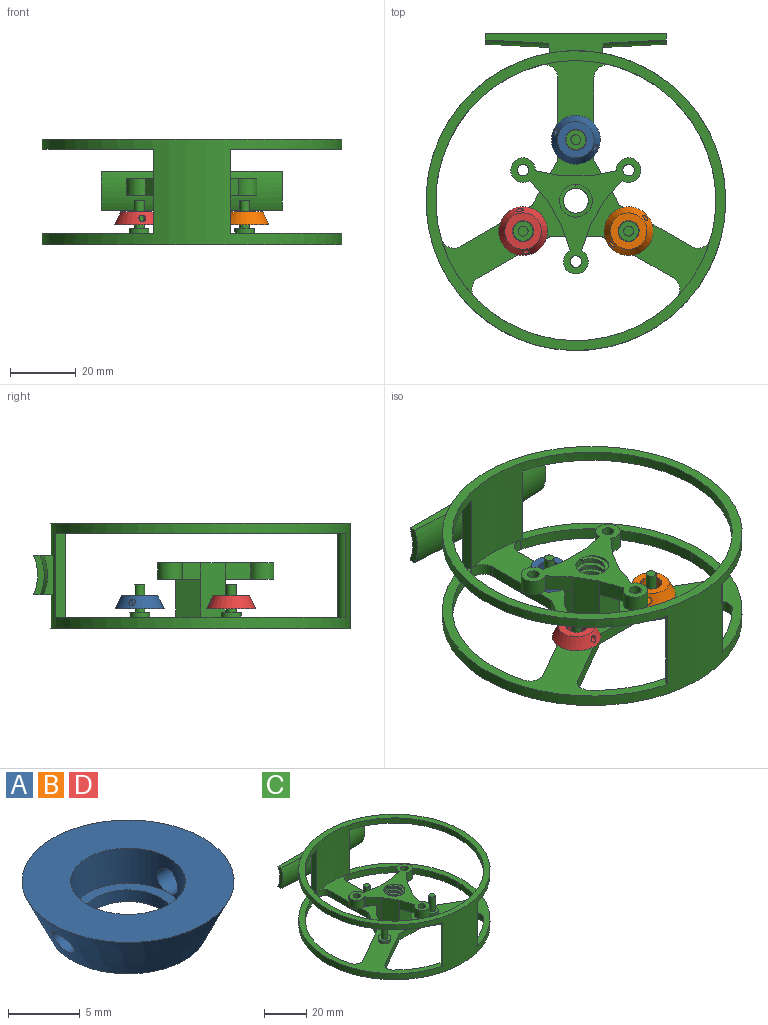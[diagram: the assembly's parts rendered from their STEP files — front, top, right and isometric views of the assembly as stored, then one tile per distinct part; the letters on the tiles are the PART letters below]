
ASSEMBLY  parts=4 mates=1
PART A: 8 faces, bbox 14.8x14.8x4 mm
  f0: cone r=7.4mm half-angle=25deg, axis (0,0,1), area 172.4mm2, adj f2,f3,f6,f7
  f1: cylinder r=4mm len=8mm, axis (0,0,1), area 69.1mm2, adj f3,f4,f6,f7
  f2: plane 11.07x11.07mm, normal (0,0,-1), area 64mm2, adj f0,f5
  f3: plane 14.8x14.8mm, normal (0,0,1), area 121.7mm2, adj f0,f1
  f4: plane 8x8mm, normal (0,0,1), area 18.1mm2, adj f1,f5
  f5: cylinder r=3.2mm len=6.4mm, axis (0,0,1), area 20.1mm2, adj f2,f4
  f6: cylinder r=1mm len=3.06mm, axis (-1,0,0), area 15.7mm2, adj f0,f1
  f7: cylinder r=1mm len=3.06mm, axis (-1,0,0), area 15.6mm2, adj f0,f1
PART B: same geometry as A
PART C: 84 faces, bbox 91.6x96.8x32.6 mm
  f0: cylinder r=42.5mm len=85mm, axis (0,0,1), area 2464.3mm2, adj f1,f2,f3,f5,f6,f7,f8,f9
  f1: cylinder r=42.5mm len=11.51mm, axis (0,0,1), area 40.8mm2, adj f0,f6,f7,f79
  f2: plane 87.9x37.23mm, normal (0,0,-1), area 347.3mm2, adj f0,f4,f9,f10,f77
  f3: plane 87.9x37.23mm, normal (0,0,-1), area 347.3mm2, adj f0,f4,f8,f11,f76
  f4: cylinder r=45.5mm len=91mm, axis (0,0,1), area 2882.7mm2, adj f2,f3,f5,f6,f7,f8,f9,f10
  f5: plane 91x91mm, normal (0,0,1), area 829.4mm2, adj f0,f4
  f6: plane 91x87.9mm, normal (0,0,1), area 1898.5mm2, adj f0,f1,f4,f8,f9,f10,f11,f12
  f7: plane 91x91mm, normal (0,0,-1), area 2234.4mm2, adj f0,f1,f4,f15,f16,f17,f18,f19
  f8: plane 25.5x2.9mm, normal (0.97,-0.26,0), area 76.5mm2, adj f0,f3,f4,f6
  f9: plane 25.5x2.9mm, normal (-0.97,-0.26,0), area 76.5mm2, adj f0,f2,f4,f6
  f10: plane 25.5x0.1mm, normal (-0.97,0.26,0), area 2.5mm2, adj f2,f4,f6,f77
  f11: plane 25.5x0.1mm, normal (0.97,0.26,0), area 2.5mm2, adj f3,f4,f6,f76
  f12: plane 11.5x7.5mm, normal (-0.87,0.5,0), area 99.6mm2, adj f6,f49,f50,f66
  f13: plane 11.5x8.66mm, normal (0,-1,0), area 99.6mm2, adj f6,f50,f51,f61
  f14: plane 11.5x7.5mm, normal (0.87,0.5,0), area 99.6mm2, adj f6,f49,f51,f56
  f15: plane 15.53x3.5mm, normal (0,-1,0), area 54.3mm2, adj f6,f7,f16,f23
  f16: plane 21.8x12.59mm, normal (0.5,-0.87,0), area 88.1mm2, adj f6,f7,f15,f83
  f17: plane 21.8x12.59mm, normal (-0.5,0.87,0), area 88.1mm2, adj f6,f7,f18,f82
  f18: plane 13.45x7.76mm, normal (-0.87,0.5,0), area 54.3mm2, adj f6,f7,f17,f19
  f19: plane 25.17x3.5mm, normal (-1,0,0), area 88.1mm2, adj f6,f7,f18,f81
  f20: plane 25.17x3.5mm, normal (1,0,0), area 88.1mm2, adj f6,f7,f21,f80
  f21: plane 13.45x7.76mm, normal (0.87,0.5,0), area 54.3mm2, adj f6,f7,f20,f22
  f22: plane 21.8x12.59mm, normal (0.5,0.87,0), area 88.1mm2, adj f6,f7,f21,f79
  f23: plane 21.8x12.59mm, normal (-0.5,-0.87,0), area 88.1mm2, adj f6,f7,f15,f78
  f24: cylinder r=3mm len=6mm, axis (0,0,1), area 28.3mm2, adj f6,f25
  f25: plane 6x6mm, normal (0,0,1), area 21.2mm2, adj f24,f26
  f26: cylinder r=1.5mm len=8.5mm, axis (0,0,1), area 80.1mm2, adj f25,f27
  f27: plane 3x3mm, normal (0,0,1), area 7.1mm2, adj f26
  f28: cylinder r=3mm len=6mm, axis (0,0,1), area 28.3mm2, adj f6,f29
  f29: plane 6x6mm, normal (0,0,1), area 21.2mm2, adj f28,f30
  f30: cylinder r=1.5mm len=8.5mm, axis (0,0,1), area 80.1mm2, adj f29,f31
  f31: plane 3x3mm, normal (0,0,1), area 7.1mm2, adj f30
  f32: cylinder r=3mm len=6mm, axis (0,0,1), area 28.3mm2, adj f6,f33
  f33: plane 6x6mm, normal (0,0,1), area 21.2mm2, adj f32,f34
  f34: cylinder r=1.5mm len=8.5mm, axis (0,0,1), area 80.1mm2, adj f33,f35
  f35: plane 3x3mm, normal (0,0,1), area 7.1mm2, adj f34
  f36: plane 1.2x0.88mm, normal (-1,0,0), area 1.1mm2, adj f38,f39,f40,f41
  f37: plane 1.2x0.88mm, normal (1,0,0), area 1.1mm2, adj f38,f39,f40,f47
  f38: cylinder r=3.8mm len=15mm, axis (0,0,-1), area 125.6mm2, adj f36,f37,f39,f40
  f39: bspline ~14.12x11.55mm, area 199.8mm2, adj f36,f37,f38,f42,f43,f44,f45,f46
  f40: bspline ~14.12x11.55mm, area 199.8mm2, adj f36,f37,f38,f41,f42,f43,f44,f45
  f41: cylinder r=5mm len=10mm, axis (0,0,1), area 37mm2, adj f36,f40,f42,f48
  f42: cylinder r=5mm len=10mm, axis (0,0,1), area 46.4mm2, adj f39,f40,f41,f43
  f43: cylinder r=5mm len=10mm, axis (0,0,1), area 46.4mm2, adj f39,f40,f42,f44
  f44: cylinder r=5mm len=10mm, axis (0,0,1), area 46.4mm2, adj f39,f40,f43,f45
  f45: cylinder r=5mm len=10mm, axis (0,0,1), area 46.4mm2, adj f39,f40,f44,f46
  f46: cylinder r=5mm len=10mm, axis (0,0,1), area 46.4mm2, adj f39,f40,f45,f47
  f47: cylinder r=5mm len=10mm, axis (0,0,1), area 194.1mm2, adj f7,f37,f39,f46
  f48: plane 39.54x35.25mm, normal (0,0,1), area 357.1mm2, adj f41,f49,f50,f51,f52,f53,f54,f55
  f49: plane 16.5x8.66mm, normal (0,1,0), area 142.9mm2, adj f6,f12,f14,f48,f53,f65
  f50: plane 16.5x7.5mm, normal (-0.87,-0.5,0), area 142.9mm2, adj f6,f12,f13,f48,f60,f63
  f51: plane 16.5x7.5mm, normal (0.87,-0.5,0), area 142.9mm2, adj f6,f13,f14,f48,f55,f58
  f52: cylinder r=3.75mm len=7.5mm, axis (0,0,1), area 99.6mm2, adj f48,f53,f55,f56
  f53: plane 7.94x5mm, normal (-0.2,0.98,0), area 40.5mm2, adj f48,f49,f52,f56
  f54: cylinder r=1.75mm len=5mm, axis (0,0,1), area 55mm2, adj f48,f56
  f55: plane 6.08x5.36mm, normal (0.75,-0.66,0), area 40.5mm2, adj f48,f51,f52,f56
  f56: plane 15.44x13mm, normal (0,0,-1), area 80.2mm2, adj f14,f52,f53,f54,f55
  f57: cylinder r=3.75mm len=7.5mm, axis (0,0,1), area 99.6mm2, adj f48,f58,f60,f61
  f58: plane 7.68x5mm, normal (0.95,-0.32,0), area 40.5mm2, adj f48,f51,f57,f61
  f59: cylinder r=1.75mm len=5mm, axis (0,0,1), area 55mm2, adj f48,f61
  f60: plane 7.68x5mm, normal (-0.95,-0.32,0), area 40.5mm2, adj f48,f50,f57,f61
  f61: plane 14.75x8.66mm, normal (0,0,-1), area 80.2mm2, adj f13,f57,f58,f59,f60
  f62: cylinder r=3.75mm len=7.5mm, axis (0,0,1), area 99.6mm2, adj f48,f63,f65,f66
  f63: plane 6.08x5.36mm, normal (-0.75,-0.66,0), area 40.5mm2, adj f48,f50,f62,f66
  f64: cylinder r=1.75mm len=5mm, axis (0,0,1), area 55mm2, adj f48,f66
  f65: plane 7.94x5mm, normal (0.2,0.98,0), area 40.5mm2, adj f48,f49,f62,f66
  f66: plane 15.44x13mm, normal (0,0,-1), area 80.2mm2, adj f12,f62,f63,f64,f65
  f67: plane 55x5.94mm, normal (0,0,1), area 186.6mm2, adj f4,f69,f70,f71,f72,f73,f74,f75
  f68: plane 55x5.94mm, normal (0,0,-1), area 186.6mm2, adj f4,f69,f70,f71,f72,f73,f74,f75
  f69: plane 12.58x3.52mm, normal (0.98,-0.17,0), area 25.5mm2, adj f4,f67,f68,f74
  f70: plane 12.58x3.52mm, normal (-0.98,-0.17,0), area 25.5mm2, adj f4,f67,f68,f71
  f71: cylinder r=15mm len=19.15mm, axis (-1,0.05,0), area 235.5mm2, adj f67,f68,f70,f75
  f72: cylinder r=15mm len=55mm, axis (1,0,0), area 679mm2, adj f67,f68,f73,f75
  f73: plane 12.03x3.28mm, normal (1,0,0), area 24mm2, adj f67,f68,f72,f74
  f74: cylinder r=15mm len=19.15mm, axis (1,0.05,0), area 235.5mm2, adj f67,f68,f69,f73
  f75: plane 12.03x3.28mm, normal (-1,0,0), area 24mm2, adj f67,f68,f71,f72
  f76: cylinder r=3mm len=25.5mm, axis (0,0,1), area 115.1mm2, adj f0,f3,f6,f11
  f77: cylinder r=3mm len=25.5mm, axis (0,0,1), area 115.1mm2, adj f0,f2,f6,f10
  f78: cylinder r=4mm len=6.26mm, axis (0,0,1), area 25.5mm2, adj f0,f6,f7,f23
  f79: cylinder r=4mm len=5.85mm, axis (0,0,1), area 25.5mm2, adj f1,f6,f7,f22
  f80: cylinder r=4mm len=4.99mm, axis (0,0,1), area 25.5mm2, adj f0,f6,f7,f20
  f81: cylinder r=4mm len=4.99mm, axis (0,0,1), area 25.5mm2, adj f0,f6,f7,f19
  f82: cylinder r=4mm len=5.85mm, axis (0,0,1), area 25.5mm2, adj f0,f6,f7,f17
  f83: cylinder r=4mm len=6.26mm, axis (0,0,1), area 25.5mm2, adj f0,f6,f7,f16
PART D: same geometry as A
PLACE A rot(axis=(0.19,0.98,0),180deg) t=(-8.14,-1.47,4.22)mm
PLACE B rot(axis=(0.94,0.33,0),180deg) t=(3.15,2.47,4.22)mm
PLACE C t=(-1.35,-2.76,1.72)mm fixed
PLACE D rot(axis=(-0.76,0.65,0),180deg) t=(0.92,-9.27,4.22)mm
MATE cylindrical A.f0 <-> C.f24  axis (0,0,1) through (-1.35,15.74,-8.53)mm
